# Revit family: Smart Sensor NeuronGrid MS660230
name_source: partatom
category: Datengeräte
units: mm (PartAtom-declared; Revit-internal decimal feet)

## family parameters
Arbeitsebenenbasiert = Nein
Beim Laden mit Abzugskörper schneiden = Nein
Bemaßung runder Anschluss = Durchmesser verwenden
Beschriftungsausrichtung beibehalten = Nein
Gemeinsam genutzt = Nein
Immer vertikal = Ja
OmniClass-Nummer = 23.85.50.17
OmniClass-Titel = Communication and Data Processing Equipment
Raumberechnungspunkt = Nein
Teiletyp = Normal

## types (1)
- Smart Sensor NeuronGrid MS660230
    Artikelnummer = MS660230
    Beschreibung = Smart Sensor NeuronGrid (Radar)
    Extension = via bus coupling
    Hersteller = MICROSENS
    Interface 1 = 2 x Sensor ports RJ 45
    Property 1 = Light intensity
    Property 2 = Movement
    Property 3 = Tempreture
    Property 4 = Humidity
    Property 5 = Integrated Beacon
    Property 6 = Air quality
    Vorgabe-Ansicht = 0 mm  [stored 0 ft]

note: [stored X ft] marks values corroborated as IEEE doubles in the binary element streams (Revit-internal decimal feet)
